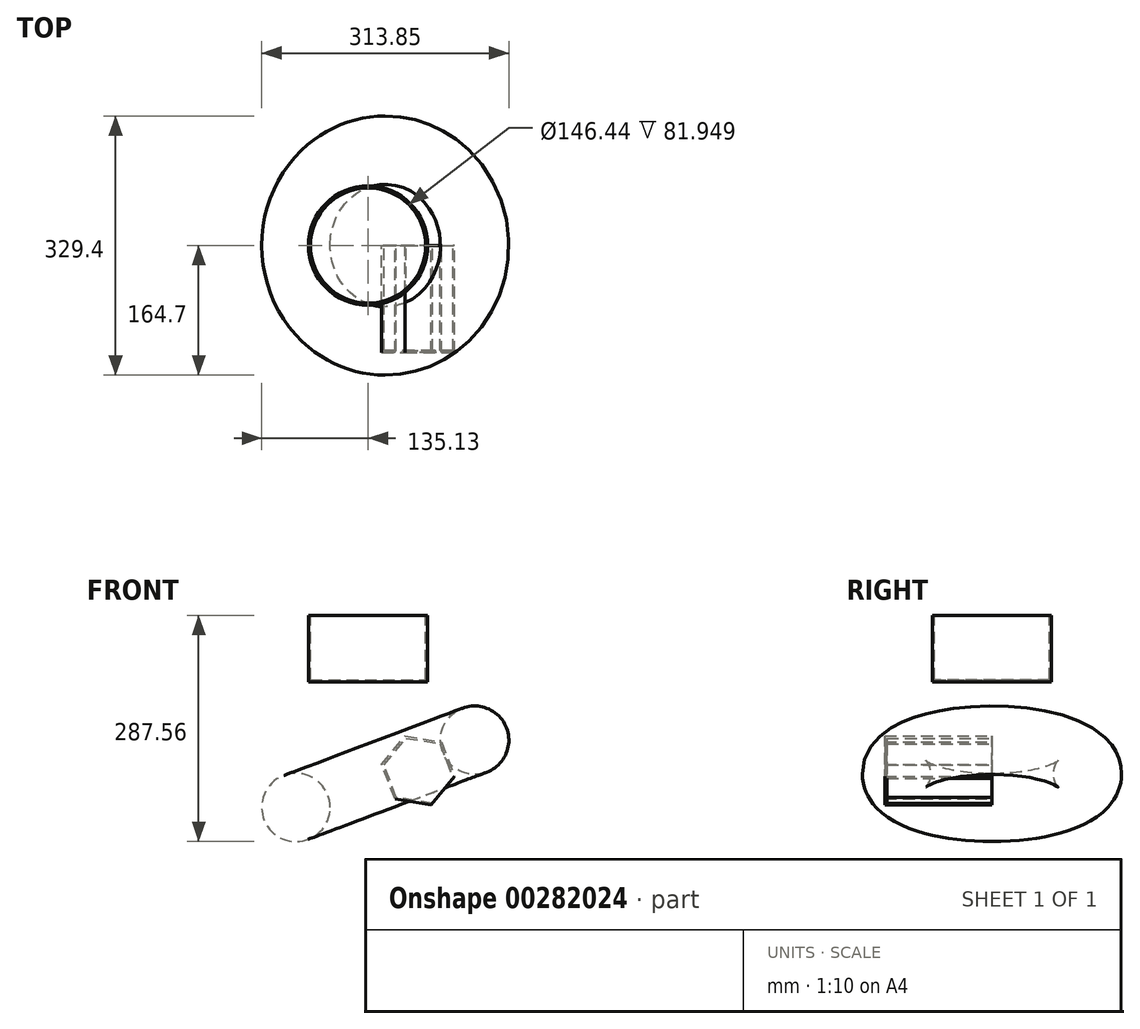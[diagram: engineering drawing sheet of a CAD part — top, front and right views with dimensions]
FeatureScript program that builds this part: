
annotation { "Feature Type Name" : "Feature", "Feature Type Description" : "" }
export const myFeature = defineFeature(function(context is Context, id is Id, definition is map)
    precondition{}
    {
        {
            var Q0;
            Q0=qCreatedBy(makeId("Front.planeOp"),FACE);
            var sketch = newSketch(context, id + "F0", { "sketchPlane" : qUnion([Q0])});
            skLineSegment(sketch, "E0.bottom", {"start": v(-75.76, 161.06) * mm, "end": v(0, 161.06) * mm});
            skLineSegment(sketch, "E0.top", {"start": v(-75.76, 76.58) * mm, "end": v(0, 76.58) * mm});
            skLineSegment(sketch, "E0.left", {"start": v(-75.76, 161.06) * mm, "end": v(-75.76, 76.58) * mm});
            skLineSegment(sketch, "E0.right", {"start": v(0, 161.06) * mm, "end": v(0, 76.58) * mm});
            skSolve(sketch);
        }
        {
            var Q0;
            Q0=makeQuery(id+"F0.imprint","IMPRINT",FACE,{"disambiguationData":[TD([[makeQuery(id+"F0.imprint","IMPRINT",EDGE,{"derivedFrom":sQuery(id+"F0.wireOp",EDGE,"E0.bottom")}),-1.0]])]});
            var Q1;
            Q1=sQuery(id+"F0.wireOp",EDGE,"E0.right");
            revolve(context, id + "F1", {"entities" : qUnion([Q0]), "axis" : qUnion([Q1]), "revolveType" : RevolveType.FULL});
        }
        {
            var Q0;
            Q0=qCreatedBy(makeId("Front.planeOp"),FACE);
            var sketch = newSketch(context, id + "F2", { "sketchPlane" : qUnion([Q0])});
            skCircle(sketch, "E1", {"center": v(-91.7, -83.06) * mm, "radius": 43.44 * mm});
            skSolve(sketch);
        }
        {
            var Q0;
            Q0=qCreatedBy(makeId("Front.planeOp"),FACE);
            var sketch = newSketch(context, id + "F3", { "sketchPlane" : qUnion([Q0])});
            skCircle(sketch, "E2.cCircle", {"center": v(63.6, -36.23) * mm, "radius": 46.86 * mm, "construction": true});
            skLineSegment(sketch, "E2.0", {"start": v(93.33, 0) * mm, "end": v(109.84, -43.86) * mm});
            skLineSegment(sketch, "E2.1", {"start": v(109.84, -43.86) * mm, "end": v(80.11, -80.08) * mm});
            skLineSegment(sketch, "E2.2", {"start": v(80.11, -80.08) * mm, "end": v(33.88, -72.45) * mm});
            skLineSegment(sketch, "E2.3", {"start": v(33.88, -72.45) * mm, "end": v(17.37, -28.6) * mm});
            skLineSegment(sketch, "E2.4", {"start": v(17.37, -28.6) * mm, "end": v(47.1, 7.63) * mm});
            skLineSegment(sketch, "E2.5", {"start": v(47.1, 7.63) * mm, "end": v(93.33, 0) * mm});
            skSolve(sketch);
        }
        {
            var Q0;
            Q0=makeQuery(id+"F3.imprint","IMPRINT",FACE,{"disambiguationData":[TD([[makeQuery(id+"F3.imprint","IMPRINT",EDGE,{"derivedFrom":sQuery(id+"F3.wireOp",EDGE,"E2.0")}),-1.0]])]});
            extrude(context, id + "F4", {"entities" : qUnion([Q0]), "depth" : 136.12 * mm});
        }
        {
            var Q0;
            Q0=makeQuery(id+"F2.imprint","IMPRINT",FACE,{"disambiguationData":[TD([[makeQuery(id+"F2.imprint","IMPRINT",EDGE,{"derivedFrom":sQuery(id+"F2.wireOp",EDGE,"E1")}),1.0]])]});
            var Q1;
            Q1=makeQuery(id+"F4.opExtrude","CAP_EDGE",EDGE,{"disambiguationData":[OSD([sQuery(id+"F3.wireOp",EDGE,"E2.3")])],"isStart":true});
            revolve(context, id + "F5", {"entities" : qUnion([Q0]), "axis" : qUnion([Q1]), "revolveType" : RevolveType.FULL});
        }
        {
            var Q0;
            Q0=makeQuery(id+"F1.opRevolve","SWEPT_FACE",FACE,{"disambiguationData":[OSD([sQuery(id+"F0.wireOp",EDGE,"E0.bottom")])]});
            shell(context, id + "F6", {"entities" : qUnion([Q0]), "thickness" : 2.54 * mm});
        }
        {
            var Q0;
            Q0=makeQuery(id+"F4.opExtrude","CAP_FACE",FACE,{"disambiguationData":[OSD([sQuery(id+"F3.wireOp",EDGE,"E2.0"),sQuery(id+"F3.wireOp",EDGE,"E2.1"),sQuery(id+"F3.wireOp",EDGE,"E2.2"),sQuery(id+"F3.wireOp",EDGE,"E2.3"),sQuery(id+"F3.wireOp",EDGE,"E2.4"),sQuery(id+"F3.wireOp",EDGE,"E2.5")])],"isStart":true});
            var Q1;
            Q1=makeQuery(id+"F4.opExtrude","SWEPT_FACE",FACE,{"disambiguationData":[OSD([sQuery(id+"F3.wireOp",EDGE,"E2.1")])]});
            shell(context, id + "F7", {"entities" : qUnion([Q0, Q1]), "thickness" : 2.54 * mm});
        }
    });
